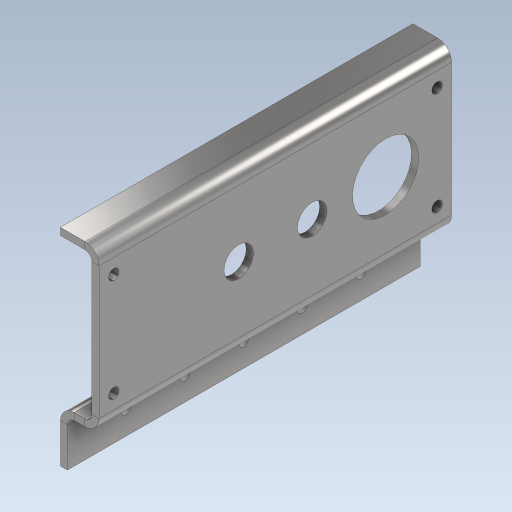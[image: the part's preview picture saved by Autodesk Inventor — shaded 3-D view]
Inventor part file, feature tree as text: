
AUTODESK INVENTOR PART (.ipt)
format: ipt  version: 2023 (Build 270158000, 158)  size: 271,360 bytes
history: native  units: in
note: dims shown in document units (in); Inventor stores cm internally (conversion verified against a paired STEP export)
features: sheet_metal_op x15, sketch x7, other x6, hole x2, projected_geometry x2
ambient origin geometry x8: Origin, YZ Plane, XZ Plane, XY Plane, X Axis, Y Axis, Z Axis, Center Point
bodies: Body1 (feature_tree)
feature tree (32):
  sheet_metal_op  "Face2"
  sheet_metal_op  "Flange1"
  sheet_metal_op  "Flange4"
  hole  "Hole2"  [1 undecoded]
  hole  "Hole1"  [1 undecoded]
  sheet_metal_op  "Face3"
  sheet_metal_op  "Flange2"
  sheet_metal_op  "Flange3"
  other  "Plate2"
  sketch  "Sketch2"  dims[d0=2.25in d1=6.0in]
  other  "Plate3"
  sheet_metal_op  "Bend1"
  sheet_metal_op  "Corner1"
  sketch  "Sketch3"  dims[d3=1.25in d4=1.25in]
  projected_geometry  "Projected Loop1"
  sketch  "Sketch4"  dims[d7=0.5in]
  other  "Plate4"
  sheet_metal_op  "Bend2"
  sketch  "Sketch5"  dims[d8=1.125in]
  other  "Plate5"
  sheet_metal_op  "Bend3"
  sheet_metal_op  "Corner2"
  sketch  "Sketch6"  dims[d10=0.12in]
  other  "Plate6"
  sheet_metal_op  "Bend4"
  sheet_metal_op  "Corner3"
  sketch  "Sketch7"  dims[d11=0.177in]
  other  "Plate7"
  sheet_metal_op  "Bend5"
  sheet_metal_op  "Corner4"
  sketch  "Sketch8"  dims[d12=5.5in d13=1.75in d14=0.5in d15=6.0in d16=0.5in d17=6.0in d18=0.12in d19=0.06in d20=0.24in d21=0.12in d22=0.6583in d23=90.0deg d24=0.12in d25=0.48in d26=0.12in d27=0.12in d28=1.0in d29=1.9685in d31=1.0in d32=0.3937in d34=1.0in d36=0.1628in d37=5.0in d38=0.22in d39=0.44in d40=0.5635in d41=0.12in d42=0.8108in d44=3.75in d45=15.748in d46=0.12in d47=0.12in d48=0.06in d49=0.24in d50=0.12in d51=0.12in d52=0.06in d53=0.24in d54=0.12in d55=0.75in d56=90.0deg d57=0.12in d58=0.48in d59=0.12in d60=0.12in d61=0.12in d62=0.06in d63=0.24in d64=0.12in d65=0.75in d66=90.0deg d67=0.12in d68=0.48in d69=0.12in d70=0.12in d71=0.75in d72=0.75in d73=0.75in d74=1.125in d75=0.5in d76=1.125in d77=1.5748in d79=2.25in d80=0.3937in d82=1.0in d84=0.12in d85=0.06in d86=0.24in d87=0.12in d88=0.7874in d89=90.0deg d90=0.12in d91=0.48in d92=0.12in d93=0.12in d94=0.3937in d95=1.0in d96=1.9685in d98=1.0in d99=0.3937in d101=1.0in d103=0.1628in d104=5.0in d105=0.375in d106=0.25in d107=0.5635in d108=1.0in d109=0.8108in]
  projected_geometry  "Projected Loop2"
note: 2 required parameter values undecoded (feature->parameter linkage not recoverable at this tier; creation-order binding heuristic only, values carry confidence <= 0.55)
